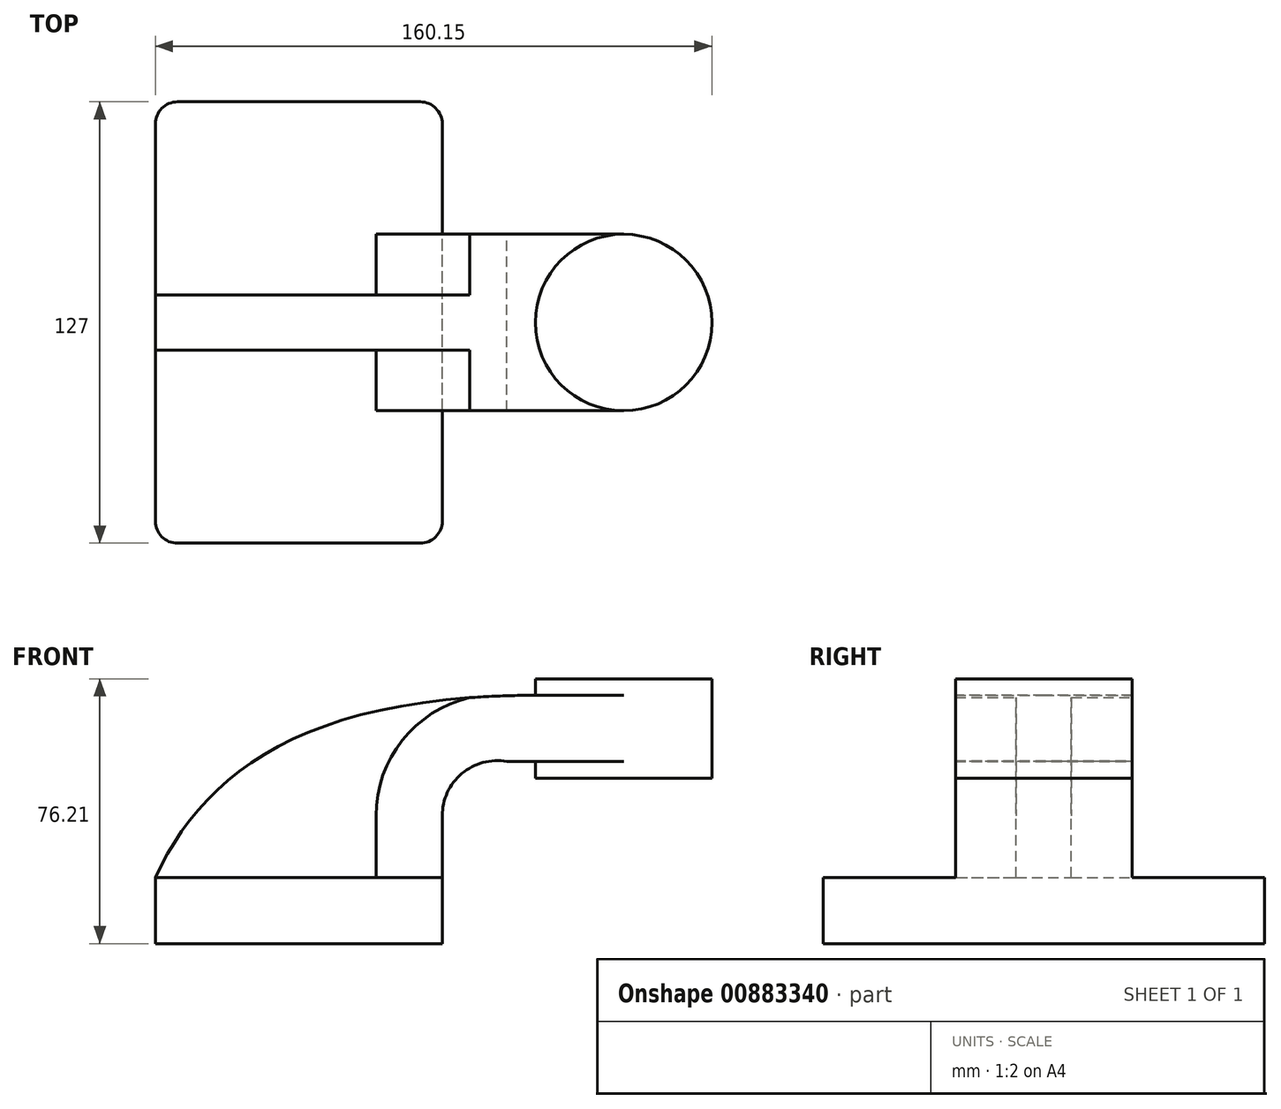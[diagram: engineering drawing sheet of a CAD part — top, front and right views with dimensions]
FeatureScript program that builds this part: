
annotation { "Feature Type Name" : "Feature", "Feature Type Description" : "" }
export const myFeature = defineFeature(function(context is Context, id is Id, definition is map)
    precondition{}
    {
        {
            var Q0;
            Q0=qCreatedBy(makeId("Front.planeOp"),FACE);
            var sketch = newSketch(context, id + "F0", { "sketchPlane" : qUnion([Q0])});
            skLineSegment(sketch, "E0.bottom", {"start": v(-41.28, -9.53) * mm, "end": v(41.28, -9.53) * mm});
            skLineSegment(sketch, "E0.top", {"start": v(-41.28, 9.53) * mm, "end": v(41.28, 9.53) * mm});
            skLineSegment(sketch, "E0.left", {"start": v(-41.28, -9.53) * mm, "end": v(-41.28, 9.53) * mm});
            skLineSegment(sketch, "E0.right", {"start": v(41.28, -9.53) * mm, "end": v(41.28, 9.53) * mm});
            skPoint(sketch, "E0.middle", {"position": v(0, 0) * mm});
            skLineSegment(sketch, "E1.bottom", {"start": v(68.07, 38.1) * mm, "end": v(118.87, 38.1) * mm});
            skLineSegment(sketch, "E1.top", {"start": v(68.07, 66.67) * mm, "end": v(118.87, 66.67) * mm});
            skLineSegment(sketch, "E1.left", {"start": v(68.07, 38.1) * mm, "end": v(68.07, 66.67) * mm});
            skLineSegment(sketch, "E1.right", {"start": v(118.87, 38.1) * mm, "end": v(118.87, 66.67) * mm});
            skPoint(sketch, "E1.middle", {"position": v(93.47, 52.39) * mm});
            skLineSegment(sketch, "E2", {"start": v(41.28, 9.52) * mm, "end": v(41.28, 27.23) * mm});
            skArc(sketch, "E3", {"start": v(41.27, 27.23) * mm, "mid": v(46.93, 39.38) * mm, "end": v(59.87, 42.88) * mm});
            skLineSegment(sketch, "E4", {"start": v(59.87, 42.88) * mm, "end": v(93.47, 42.88) * mm});
            skLineSegment(sketch, "E5.0", {"start": v(61.19, 61.93) * mm, "end": v(93.47, 61.93) * mm});
            skArc(sketch, "E5.1", {"start": v(22.22, 27.23) * mm, "mid": v(33.93, 53.32) * mm, "end": v(61.19, 61.93) * mm});
            skLineSegment(sketch, "E5.2", {"start": v(22.22, 9.52) * mm, "end": v(22.22, 27.23) * mm});
            skLineSegment(sketch, "E6", {"start": v(93.47, 38.1) * mm, "end": v(93.47, 66.67) * mm});
            skFitSpline(sketch, "E7", {"points": [v(-41.28, 9.53) * mm, v(68.07, 61.93) * mm], "startDerivative": vector(41.14, 87.62) * mm, "endDerivative": vector(204.22, 0.4) * mm});
            skSolve(sketch);
        }
        {
            var Q0;
            Q0=makeQuery(id+"F0.imprint","IMPRINT",FACE,{"disambiguationData":[TD([[makeQuery(id+"F0.imprint","IMPRINT",EDGE,{"derivedFrom":sQuery(id+"F0.wireOp",EDGE,"E0.bottom")}),1.0]])]});
            extrude(context, id + "F1", {"entities" : qUnion([Q0]), "endBound" : BoundingType.SYMMETRIC, "depth" : 127 * mm, "offsetDistance" : 25.4 * mm});
        }
        {
            var Q0;
            {var subQ1=sQuery(id+"F0.wireOp",EDGE,"E2");Q0=makeQuery(id+"F0.imprint","IMPRINT",FACE,{"disambiguationData":[TD([[makeQuery(id+"F0.imprint","IMPRINT",EDGE,{"derivedFrom":subQ1}),1.0]])]});}
            var Q1;
            {var subQ3=sQuery(id+"F0.wireOp",EDGE,"E4");var subQ5=sQuery(id+"F0.wireOp",EDGE,"E6");var subQ6=makeQuery(id+"F0.imprint","INTERSECT",VERTEX,{"derivedFrom":[subQ3,subQ5]});Q1=makeQuery(id+"F0.imprint","IMPRINT",FACE,{"disambiguationData":[TD([[makeQuery(id+"F0.imprint","IMPRINT",EDGE,{"disambiguationData":[TD([[subQ6,1.0]])],"derivedFrom":subQ3}),1.0]])]});}
            extrude(context, id + "F2", {"entities" : qUnion([Q0, Q1]), "operationType" : NewBodyOperationType.ADD, "endBound" : BoundingType.SYMMETRIC, "depth" : 50.8 * mm, "offsetDistance" : 25.4 * mm});
        }
        {
            var Q0;
            {var subQ3=sQuery(id+"F0.wireOp",EDGE,"E5.2");Q0=makeQuery(id+"F0.imprint","IMPRINT",FACE,{"disambiguationData":[TD([[makeQuery(id+"F0.imprint","IMPRINT",EDGE,{"derivedFrom":subQ3}),1.0]])]});}
            extrude(context, id + "F3", {"entities" : qUnion([Q0]), "operationType" : NewBodyOperationType.ADD, "endBound" : BoundingType.SYMMETRIC, "depth" : 15.88 * mm, "offsetDistance" : 25.4 * mm});
        }
        {
            var Q0;
            {var subQ4=sQuery(id+"F0.wireOp",EDGE,"E1.right");Q0=makeQuery(id+"F0.imprint","IMPRINT",FACE,{"disambiguationData":[TD([[makeQuery(id+"F0.imprint","IMPRINT",EDGE,{"derivedFrom":subQ4}),1.0]])]});}
            var Q1;
            Q1=sQuery(id+"F0.wireOp",EDGE,"E6");
            revolve(context, id + "F4", {"operationType" : NewBodyOperationType.ADD, "surfaceOperationType" : NewSurfaceOperationType.NEW, "entities" : qUnion([Q0]), "axis" : qUnion([Q1]), "revolveType" : RevolveType.FULL});
        }
        {
            var Q0;
            Q0=makeQuery(id+"F1.opExtrude","CAP_EDGE",EDGE,{"disambiguationData":[OSD([sQuery(id+"F0.wireOp",EDGE,"E0.left")])],"isStart":false});
            var Q1;
            Q1=makeQuery(id+"F1.opExtrude","CAP_EDGE",EDGE,{"disambiguationData":[OSD([sQuery(id+"F0.wireOp",EDGE,"E0.right")])],"isStart":false});
            var Q2;
            Q2=makeQuery(id+"F1.opExtrude","CAP_EDGE",EDGE,{"disambiguationData":[OSD([sQuery(id+"F0.wireOp",EDGE,"E0.right")])],"isStart":true});
            var Q3;
            Q3=makeQuery(id+"F1.opExtrude","CAP_EDGE",EDGE,{"disambiguationData":[OSD([sQuery(id+"F0.wireOp",EDGE,"E0.left")])],"isStart":true});
            fillet(context, id + "F5", {"entities" : qUnion([Q0, Q1, Q2, Q3]), "radius" : 6.35 * mm, "tangentPropagation" : true, "allowEdgeOverflow" : false});
        }
    });
